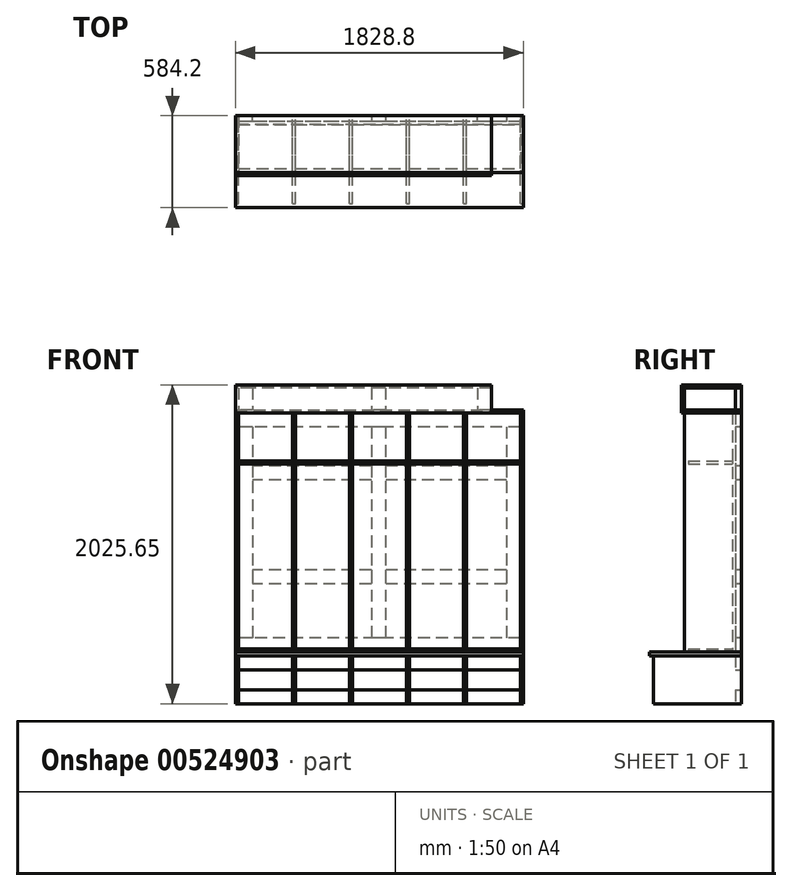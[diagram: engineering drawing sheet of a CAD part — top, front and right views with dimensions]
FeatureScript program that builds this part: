
annotation { "Feature Type Name" : "Feature", "Feature Type Description" : "" }
export const myFeature = defineFeature(function(context is Context, id is Id, definition is map)
    precondition{}
    {
        {
            var Q0;
            Q0=qCreatedBy(makeId("Front.planeOp"),FACE);
            var sketch = newSketch(context, id + "F0", { "sketchPlane" : qUnion([Q0])});
            skLineSegment(sketch, "E0.bottom", {"start": v(-620.12, 1849.45) * mm, "end": v(-601.07, 1849.45) * mm});
            skLineSegment(sketch, "E0.left", {"start": v(-620.12, 1849.45) * mm, "end": v(-620.12, 330.2) * mm});
            skLineSegment(sketch, "E0.right", {"start": v(-601.07, 1849.45) * mm, "end": v(-601.07, 330.2) * mm});
            skLineSegment(sketch, "E1.bottom", {"start": v(-258.17, 1849.45) * mm, "end": v(-239.12, 1849.45) * mm});
            skLineSegment(sketch, "E1.left", {"start": v(-258.17, 1849.45) * mm, "end": v(-258.17, 330.2) * mm});
            skLineSegment(sketch, "E1.right", {"start": v(-239.12, 1849.45) * mm, "end": v(-239.12, 330.2) * mm});
            skLineSegment(sketch, "E2.bottom", {"start": v(103.78, 1849.45) * mm, "end": v(122.83, 1849.45) * mm});
            skLineSegment(sketch, "E2.left", {"start": v(103.78, 1849.45) * mm, "end": v(103.78, 330.2) * mm});
            skLineSegment(sketch, "E2.right", {"start": v(122.83, 1849.45) * mm, "end": v(122.83, 330.2) * mm});
            skLineSegment(sketch, "E3.bottom", {"start": v(465.73, 1849.45) * mm, "end": v(484.78, 1849.45) * mm});
            skLineSegment(sketch, "E3.left", {"start": v(465.73, 1849.45) * mm, "end": v(465.73, 330.2) * mm});
            skLineSegment(sketch, "E3.right", {"start": v(484.78, 1849.45) * mm, "end": v(484.78, 330.2) * mm});
            skLineSegment(sketch, "E4.trimOffspring", {"start": v(465.73, 330.2) * mm, "end": v(484.78, 330.2) * mm});
            skLineSegment(sketch, "E5.trimOffspring", {"start": v(103.78, 330.2) * mm, "end": v(122.83, 330.2) * mm});
            skLineSegment(sketch, "E6.trimOffspring", {"start": v(-258.17, 330.2) * mm, "end": v(-239.12, 330.2) * mm});
            skLineSegment(sketch, "E7.trimOffspring", {"start": v(-620.12, 330.2) * mm, "end": v(-601.07, 330.2) * mm});
            skSolve(sketch);
        }
        {
            var Q0;
            Q0 = qSketchRegion(id + "F0", true);
            extrude(context, id + "F1", {"entities" : qUnion([Q0]), "depth" : 285.75 * mm, "offsetDistance" : 25.4 * mm, "hasSecondDirection" : true, "secondDirectionOppositeDirection" : true, "secondDirectionDepth" : 19.05 * mm});
        }
        {
            var Q0;
            Q0=qCreatedBy(makeId("Front.planeOp"),FACE);
            var sketch = newSketch(context, id + "F2", { "sketchPlane" : qUnion([Q0])});
            skLineSegment(sketch, "E8.bottom", {"start": v(-982.07, 330.2) * mm, "end": v(846.73, 330.2) * mm});
            skLineSegment(sketch, "E8.top", {"start": v(-982.07, 304.8) * mm, "end": v(846.73, 304.8) * mm});
            skLineSegment(sketch, "E8.left", {"start": v(-982.07, 330.2) * mm, "end": v(-982.07, 304.8) * mm});
            skLineSegment(sketch, "E8.right", {"start": v(846.73, 330.2) * mm, "end": v(846.73, 304.8) * mm});
            skSolve(sketch);
        }
        {
            var Q0;
            Q0 = qSketchRegion(id + "F2", true);
            extrude(context, id + "F3", {"entities" : qUnion([Q0]), "oppositeDirection" : true, "depth" : 76.2 * mm, "offsetDistance" : 25.4 * mm, "hasSecondDirection" : true, "secondDirectionOppositeDirection" : false, "secondDirectionDepth" : 508 * mm});
        }
        {
            var Q0;
            Q0=qCreatedBy(makeId("Front.planeOp"),FACE);
            var sketch = newSketch(context, id + "F4", { "sketchPlane" : qUnion([Q0])});
            skLineSegment(sketch, "E9.bottom", {"start": v(-982.07, 304.8) * mm, "end": v(-963.02, 304.8) * mm});
            skLineSegment(sketch, "E9.top", {"start": v(-982.07, 0) * mm, "end": v(-963.02, 0) * mm});
            skLineSegment(sketch, "E9.left", {"start": v(-982.07, 304.8) * mm, "end": v(-982.07, 0) * mm});
            skLineSegment(sketch, "E9.right", {"start": v(-963.02, 304.8) * mm, "end": v(-963.02, 0) * mm});
            skLineSegment(sketch, "E10.bottom", {"start": v(-620.12, 304.8) * mm, "end": v(-601.07, 304.8) * mm});
            skLineSegment(sketch, "E10.top", {"start": v(-620.12, 0) * mm, "end": v(-601.07, 0) * mm});
            skLineSegment(sketch, "E10.left", {"start": v(-620.12, 304.8) * mm, "end": v(-620.12, 0) * mm});
            skLineSegment(sketch, "E10.right", {"start": v(-601.07, 304.8) * mm, "end": v(-601.07, 0) * mm});
            skLineSegment(sketch, "E11.bottom", {"start": v(-258.17, 304.8) * mm, "end": v(-239.12, 304.8) * mm});
            skLineSegment(sketch, "E11.top", {"start": v(-258.17, 0) * mm, "end": v(-239.12, 0) * mm});
            skLineSegment(sketch, "E11.left", {"start": v(-258.17, 304.8) * mm, "end": v(-258.17, 0) * mm});
            skLineSegment(sketch, "E11.right", {"start": v(-239.12, 304.8) * mm, "end": v(-239.12, 0) * mm});
            skLineSegment(sketch, "E12.bottom", {"start": v(103.78, 304.8) * mm, "end": v(122.83, 304.8) * mm});
            skLineSegment(sketch, "E12.top", {"start": v(103.78, 0) * mm, "end": v(122.83, 0) * mm});
            skLineSegment(sketch, "E12.left", {"start": v(103.78, 304.8) * mm, "end": v(103.78, 0) * mm});
            skLineSegment(sketch, "E12.right", {"start": v(122.83, 304.8) * mm, "end": v(122.83, 0) * mm});
            skLineSegment(sketch, "E13.bottom", {"start": v(465.73, 304.8) * mm, "end": v(484.78, 304.8) * mm});
            skLineSegment(sketch, "E13.top", {"start": v(465.73, 0) * mm, "end": v(484.78, 0) * mm});
            skLineSegment(sketch, "E13.left", {"start": v(465.73, 304.8) * mm, "end": v(465.73, 0) * mm});
            skLineSegment(sketch, "E13.right", {"start": v(484.78, 304.8) * mm, "end": v(484.78, 0) * mm});
            skLineSegment(sketch, "E14.bottom", {"start": v(827.68, 304.8) * mm, "end": v(846.73, 304.8) * mm});
            skLineSegment(sketch, "E14.top", {"start": v(827.68, 0) * mm, "end": v(846.73, 0) * mm});
            skLineSegment(sketch, "E14.left", {"start": v(827.68, 304.8) * mm, "end": v(827.68, 0) * mm});
            skLineSegment(sketch, "E14.right", {"start": v(846.73, 304.8) * mm, "end": v(846.73, 0) * mm});
            skSolve(sketch);
        }
        {
            var Q0;
            Q0 = qSketchRegion(id + "F4", true);
            extrude(context, id + "F5", {"entities" : qUnion([Q0]), "depth" : 482.6 * mm, "offsetDistance" : 25.4 * mm, "hasSecondDirection" : true, "secondDirectionOppositeDirection" : true, "secondDirectionDepth" : 76.2 * mm});
        }
        {
            var Q0;
            Q0=makeQuery(id+"F5.opExtrude","CAP_FACE",FACE,{"disambiguationData":[OSD([sQuery(id+"F4.wireOp",EDGE,"E14.bottom"),sQuery(id+"F4.wireOp",EDGE,"E14.top"),sQuery(id+"F4.wireOp",EDGE,"E14.left"),sQuery(id+"F4.wireOp",EDGE,"E14.right")])],"isStart":true});
            var sketch = newSketch(context, id + "F6", { "sketchPlane" : qUnion([Q0])});
            skLineSegment(sketch, "E15.bottom", {"start": v(-827.68, 88.9) * mm, "end": v(963.02, 88.9) * mm});
            skLineSegment(sketch, "E15.top", {"start": v(-827.68, 0) * mm, "end": v(963.02, 0) * mm});
            skLineSegment(sketch, "E15.left", {"start": v(-827.68, 88.9) * mm, "end": v(-827.68, 0) * mm});
            skLineSegment(sketch, "E15.right", {"start": v(963.02, 88.9) * mm, "end": v(963.02, 0) * mm});
            skLineSegment(sketch, "E16.bottom", {"start": v(-827.68, 419.1) * mm, "end": v(963.02, 419.1) * mm});
            skLineSegment(sketch, "E16.top", {"start": v(-827.68, 330.2) * mm, "end": v(963.02, 330.2) * mm});
            skLineSegment(sketch, "E17.top", {"start": v(-827.68, 1758.95) * mm, "end": v(963.02, 1758.95) * mm});
            skLineSegment(sketch, "E18", {"start": v(-827.68, 1847.85) * mm, "end": v(-827.68, 1758.95) * mm});
            skLineSegment(sketch, "E19", {"start": v(963.02, 1847.85) * mm, "end": v(963.02, 1758.95) * mm});
            skLineSegment(sketch, "E20.trimOffspring", {"start": v(963.02, 419.1) * mm, "end": v(963.02, 330.2) * mm});
            skLineSegment(sketch, "E21.trimOffspring", {"start": v(-827.68, 419.1) * mm, "end": v(-827.68, 330.2) * mm});
            skLineSegment(sketch, "E22", {"start": v(-827.68, 1847.85) * mm, "end": v(963.02, 1847.85) * mm});
            skLineSegment(sketch, "E23.bottom", {"start": v(-827.68, 304.8) * mm, "end": v(963.02, 304.8) * mm});
            skLineSegment(sketch, "E23.top", {"start": v(-827.68, 215.9) * mm, "end": v(963.02, 215.9) * mm});
            skLineSegment(sketch, "E23.left", {"start": v(-827.68, 304.8) * mm, "end": v(-827.68, 215.9) * mm});
            skLineSegment(sketch, "E23.right", {"start": v(963.02, 304.8) * mm, "end": v(963.02, 215.9) * mm});
            skSolve(sketch);
        }
        {
            var Q0;
            Q0=makeQuery(id+"F6.imprint","IMPRINT",FACE,{"disambiguationData":[TD([[makeQuery(id+"F6.imprint","IMPRINT",EDGE,{"derivedFrom":sQuery(id+"F6.wireOp",EDGE,"E17.top")}),1.0]])]});
            var Q1;
            Q1=makeQuery(id+"F6.imprint","IMPRINT",FACE,{"disambiguationData":[TD([[makeQuery(id+"F6.imprint","IMPRINT",EDGE,{"derivedFrom":sQuery(id+"F6.wireOp",EDGE,"E16.bottom")}),-1.0]])]});
            var Q2;
            Q2=makeQuery(id+"F6.imprint","IMPRINT",FACE,{"disambiguationData":[TD([[makeQuery(id+"F6.imprint","IMPRINT",EDGE,{"derivedFrom":sQuery(id+"F6.wireOp",EDGE,"E15.bottom")}),-1.0]])]});
            var Q3;
            Q3=makeQuery(id+"F6.imprint","IMPRINT",FACE,{"disambiguationData":[TD([[makeQuery(id+"F6.imprint","IMPRINT",EDGE,{"derivedFrom":sQuery(id+"F6.wireOp",EDGE,"E23.bottom")}),-1.0]])]});
            extrude(context, id + "F7", {"entities" : qUnion([Q0, Q1, Q2, Q3]), "oppositeDirection" : true, "depth" : 38.1 * mm, "offsetDistance" : 25.4 * mm});
        }
        {
            var Q0;
            Q0=makeQuery(id+"F1.opExtrude","CAP_FACE",FACE,{"disambiguationData":[OSD([sQuery(id+"F0.wireOp",EDGE,"E0.bottom"),sQuery(id+"F0.wireOp",EDGE,"E0.left"),sQuery(id+"F0.wireOp",EDGE,"E0.right"),sQuery(id+"F0.wireOp",EDGE,"E7.trimOffspring")])],"isStart":false});
            var sketch = newSketch(context, id + "F8", { "sketchPlane" : qUnion([Q0])});
            skLineSegment(sketch, "E24.bottom", {"start": v(-963.02, 330.2) * mm, "end": v(-982.07, 330.2) * mm});
            skLineSegment(sketch, "E24.top", {"start": v(-963.02, 1847.85) * mm, "end": v(-982.07, 1847.85) * mm});
            skLineSegment(sketch, "E24.left", {"start": v(-963.02, 330.2) * mm, "end": v(-963.02, 1847.85) * mm});
            skLineSegment(sketch, "E24.right", {"start": v(-982.07, 330.2) * mm, "end": v(-982.07, 1847.85) * mm});
            skLineSegment(sketch, "E25.bottom", {"start": v(827.68, 330.2) * mm, "end": v(846.73, 330.2) * mm});
            skLineSegment(sketch, "E25.top", {"start": v(827.68, 1847.85) * mm, "end": v(846.73, 1847.85) * mm});
            skLineSegment(sketch, "E25.left", {"start": v(827.68, 330.2) * mm, "end": v(827.68, 1847.85) * mm});
            skLineSegment(sketch, "E25.right", {"start": v(846.73, 330.2) * mm, "end": v(846.73, 1847.85) * mm});
            skSolve(sketch);
        }
        {
            var Q0;
            Q0 = qSketchRegion(id + "F8", true);
            extrude(context, id + "F9", {"entities" : qUnion([Q0]), "oppositeDirection" : true, "depth" : 361.95 * mm, "offsetDistance" : 25.4 * mm});
        }
        {
            var Q0;
            Q0=makeQuery(id+"F3.opExtrude","SWEPT_FACE",FACE,{"disambiguationData":[OSD([sQuery(id+"F2.wireOp",EDGE,"E8.bottom")])]});
            var sketch = newSketch(context, id + "F10", { "sketchPlane" : qUnion([Q0])});
            skLineSegment(sketch, "E26.bottom", {"start": v(-963.02, 38.1) * mm, "end": v(827.68, 38.1) * mm});
            skLineSegment(sketch, "E26.top", {"start": v(-963.02, 19.05) * mm, "end": v(827.68, 19.05) * mm});
            skLineSegment(sketch, "E26.left", {"start": v(-963.02, 38.1) * mm, "end": v(-963.02, 19.05) * mm});
            skLineSegment(sketch, "E26.right", {"start": v(827.68, 38.1) * mm, "end": v(827.68, 19.05) * mm});
            skSolve(sketch);
        }
        {
            var Q0;
            Q0=makeQuery(id+"F10.imprint","IMPRINT",FACE,{"disambiguationData":[TD([[makeQuery(id+"F10.imprint","IMPRINT",EDGE,{"derivedFrom":sQuery(id+"F10.wireOp",EDGE,"E26.bottom")}),-1.0]])]});
            var Q1;
            Q1=makeQuery(id+"F7.opExtrude","SWEPT_FACE",FACE,{"disambiguationData":[OSD([sQuery(id+"F6.wireOp",EDGE,"E22")])]});
            extrude(context, id + "F11", {"entities" : qUnion([Q0]), "endBound" : BoundingType.UP_TO_SURFACE, "depth" : 25.4 * mm, "endBoundEntityFace" : qUnion([Q1]), "offsetDistance" : 25.4 * mm});
        }
        {
            var Q0;
            Q0=makeQuery(id+"F11.opExtrude","SWEPT_FACE",FACE,{"disambiguationData":[OSD([sQuery(id+"F10.wireOp",EDGE,"E26.top")])]});
            var sketch = newSketch(context, id + "F12", { "sketchPlane" : qUnion([Q0])});
            skLineSegment(sketch, "E27.bottom", {"start": v(-963.02, 1543.05) * mm, "end": v(-620.12, 1543.05) * mm});
            skLineSegment(sketch, "E27.top", {"start": v(-963.02, 1524) * mm, "end": v(-620.12, 1524) * mm});
            skLineSegment(sketch, "E27.left", {"start": v(-963.02, 1543.05) * mm, "end": v(-963.02, 1524) * mm});
            skLineSegment(sketch, "E27.right", {"start": v(-620.12, 1543.05) * mm, "end": v(-620.12, 1524) * mm});
            skLineSegment(sketch, "E28.bottom", {"start": v(-601.07, 1543.05) * mm, "end": v(-258.17, 1543.05) * mm});
            skLineSegment(sketch, "E28.top", {"start": v(-601.07, 1524) * mm, "end": v(-258.17, 1524) * mm});
            skLineSegment(sketch, "E28.left", {"start": v(-601.07, 1543.05) * mm, "end": v(-601.07, 1524) * mm});
            skLineSegment(sketch, "E28.right", {"start": v(-258.17, 1543.05) * mm, "end": v(-258.17, 1524) * mm});
            skLineSegment(sketch, "E29.bottom", {"start": v(-239.12, 1543.05) * mm, "end": v(103.78, 1543.05) * mm});
            skLineSegment(sketch, "E29.top", {"start": v(-239.12, 1524) * mm, "end": v(103.78, 1524) * mm});
            skLineSegment(sketch, "E29.left", {"start": v(-239.12, 1543.05) * mm, "end": v(-239.12, 1524) * mm});
            skLineSegment(sketch, "E29.right", {"start": v(103.78, 1543.05) * mm, "end": v(103.78, 1524) * mm});
            skLineSegment(sketch, "E30.bottom", {"start": v(122.83, 1543.05) * mm, "end": v(465.73, 1543.05) * mm});
            skLineSegment(sketch, "E30.top", {"start": v(122.83, 1524) * mm, "end": v(465.73, 1524) * mm});
            skLineSegment(sketch, "E30.left", {"start": v(122.83, 1543.05) * mm, "end": v(122.83, 1524) * mm});
            skLineSegment(sketch, "E30.right", {"start": v(465.73, 1543.05) * mm, "end": v(465.73, 1524) * mm});
            skLineSegment(sketch, "E31.bottom", {"start": v(484.78, 1543.05) * mm, "end": v(827.68, 1543.05) * mm});
            skLineSegment(sketch, "E31.top", {"start": v(484.78, 1524) * mm, "end": v(827.68, 1524) * mm});
            skLineSegment(sketch, "E31.left", {"start": v(484.78, 1543.05) * mm, "end": v(484.78, 1524) * mm});
            skLineSegment(sketch, "E31.right", {"start": v(827.68, 1543.05) * mm, "end": v(827.68, 1524) * mm});
            skSolve(sketch);
        }
        {
            var Q0;
            Q0 = qSketchRegion(id + "F12", true);
            extrude(context, id + "F13", {"entities" : qUnion([Q0]), "depth" : 279.4 * mm, "offsetDistance" : 25.4 * mm});
        }
        {
            var Q0;
            Q0=makeQuery(id+"F9.opExtrude","CAP_FACE",FACE,{"disambiguationData":[OSD([sQuery(id+"F8.wireOp",EDGE,"E24.bottom"),sQuery(id+"F8.wireOp",EDGE,"E24.top"),sQuery(id+"F8.wireOp",EDGE,"E24.left"),sQuery(id+"F8.wireOp",EDGE,"E24.right")])],"isStart":true});
            var sketch = newSketch(context, id + "F14", { "sketchPlane" : qUnion([Q0])});
            skLineSegment(sketch, "E32.bottom", {"start": v(-982.07, 1847.85) * mm, "end": v(643.53, 1847.85) * mm});
            skLineSegment(sketch, "E32.top", {"start": v(-982.07, 2025.65) * mm, "end": v(643.53, 2025.65) * mm});
            skLineSegment(sketch, "E32.left", {"start": v(-982.07, 1847.85) * mm, "end": v(-982.07, 2025.65) * mm});
            skLineSegment(sketch, "E32.right", {"start": v(643.53, 1847.85) * mm, "end": v(643.53, 2025.65) * mm});
            skSolve(sketch);
        }
        {
            var Q0;
            Q0=makeQuery(id+"F14.imprint","IMPRINT",FACE,{"disambiguationData":[TD([[makeQuery(id+"F14.imprint","IMPRINT",EDGE,{"derivedFrom":sQuery(id+"F14.wireOp",EDGE,"E32.top")}),-1.0]])]});
            extrude(context, id + "F15", {"entities" : qUnion([Q0]), "depth" : 19.05 * mm, "offsetDistance" : 25.4 * mm});
        }
        {
            var Q0;
            Q0=makeQuery(id+"F15.opExtrude","CAP_FACE",FACE,{"disambiguationData":[OSD([sQuery(id+"F14.wireOp",EDGE,"E32.bottom"),sQuery(id+"F14.wireOp",EDGE,"E32.top"),sQuery(id+"F14.wireOp",EDGE,"E32.left"),sQuery(id+"F14.wireOp",EDGE,"E32.right")])],"isStart":true});
            var sketch = newSketch(context, id + "F16", { "sketchPlane" : qUnion([Q0])});
            skLineSegment(sketch, "E33.bottom", {"start": v(-643.53, 2025.65) * mm, "end": v(982.07, 2025.65) * mm});
            skLineSegment(sketch, "E33.top", {"start": v(-643.53, 2006.6) * mm, "end": v(982.07, 2006.6) * mm});
            skLineSegment(sketch, "E33.left", {"start": v(-643.53, 2025.65) * mm, "end": v(-643.53, 2006.6) * mm});
            skLineSegment(sketch, "E33.right", {"start": v(982.07, 2025.65) * mm, "end": v(982.07, 2006.6) * mm});
            skLineSegment(sketch, "E34.bottom", {"start": v(982.07, 1847.85) * mm, "end": v(-846.73, 1847.85) * mm});
            skLineSegment(sketch, "E34.top", {"start": v(982.07, 1866.9) * mm, "end": v(-846.73, 1866.9) * mm});
            skLineSegment(sketch, "E34.left", {"start": v(982.07, 1847.85) * mm, "end": v(982.07, 1866.9) * mm});
            skLineSegment(sketch, "E34.right", {"start": v(-846.73, 1847.85) * mm, "end": v(-846.73, 1866.9) * mm});
            skSolve(sketch);
        }
        {
            var Q0;
            Q0 = qSketchRegion(id + "F16", true);
            var Q1;
            Q1=makeQuery(id+"F7.opExtrude","CAP_FACE",FACE,{"disambiguationData":[OSD([sQuery(id+"F6.wireOp",EDGE,"E17.top"),sQuery(id+"F6.wireOp",EDGE,"E18"),sQuery(id+"F6.wireOp",EDGE,"E19"),sQuery(id+"F6.wireOp",EDGE,"E22")])],"isStart":true});
            extrude(context, id + "F17", {"entities" : qUnion([Q0]), "endBound" : BoundingType.UP_TO_SURFACE, "depth" : 285.75 * mm, "endBoundEntityFace" : qUnion([Q1]), "offsetDistance" : 25.4 * mm});
        }
        {
            var Q0;
            Q0=makeQuery(id+"F11.opExtrude","SWEPT_FACE",FACE,{"disambiguationData":[OSD([sQuery(id+"F10.wireOp",EDGE,"E26.bottom")])]});
            var sketch = newSketch(context, id + "F18", { "sketchPlane" : qUnion([Q0])});
            skLineSegment(sketch, "E35.bottom", {"start": v(-827.68, 1758.95) * mm, "end": v(-738.78, 1758.95) * mm});
            skLineSegment(sketch, "E35.top", {"start": v(-827.68, 419.1) * mm, "end": v(-738.78, 419.1) * mm});
            skLineSegment(sketch, "E35.left", {"start": v(-827.68, 1758.95) * mm, "end": v(-827.68, 419.1) * mm});
            skLineSegment(sketch, "E35.right", {"start": v(-738.78, 1758.95) * mm, "end": v(-738.78, 419.1) * mm});
            skLineSegment(sketch, "E36.bottom", {"start": v(874.12, 1758.95) * mm, "end": v(963.02, 1758.95) * mm});
            skLineSegment(sketch, "E36.top", {"start": v(874.12, 419.1) * mm, "end": v(963.02, 419.1) * mm});
            skLineSegment(sketch, "E36.left", {"start": v(874.12, 1758.95) * mm, "end": v(874.12, 419.1) * mm});
            skLineSegment(sketch, "E36.right", {"start": v(963.02, 1758.95) * mm, "end": v(963.02, 419.1) * mm});
            skLineSegment(sketch, "E37.bottom", {"start": v(29.57, 1758.95) * mm, "end": v(118.47, 1758.95) * mm});
            skLineSegment(sketch, "E37.top", {"start": v(29.57, 419.1) * mm, "end": v(118.47, 419.1) * mm});
            skLineSegment(sketch, "E37.left", {"start": v(29.57, 1758.95) * mm, "end": v(29.57, 419.1) * mm});
            skLineSegment(sketch, "E37.right", {"start": v(118.47, 1758.95) * mm, "end": v(118.47, 419.1) * mm});
            skSolve(sketch);
        }
        {
            var Q0;
            Q0 = qSketchRegion(id + "F18", true);
            extrude(context, id + "F19", {"entities" : qUnion([Q0]), "depth" : 38.1 * mm, "offsetDistance" : 25.4 * mm});
        }
        {
            var Q0;
            Q0=makeQuery(id+"F11.opExtrude","SWEPT_FACE",FACE,{"disambiguationData":[OSD([sQuery(id+"F10.wireOp",EDGE,"E26.bottom")])]});
            var sketch = newSketch(context, id + "F20", { "sketchPlane" : qUnion([Q0])});
            skLineSegment(sketch, "E38.bottom", {"start": v(-738.78, 1511.3) * mm, "end": v(29.57, 1511.3) * mm});
            skLineSegment(sketch, "E38.top", {"start": v(-738.78, 1422.4) * mm, "end": v(29.57, 1422.4) * mm});
            skLineSegment(sketch, "E38.left", {"start": v(-738.78, 1511.3) * mm, "end": v(-738.78, 1422.4) * mm});
            skLineSegment(sketch, "E39.bottom", {"start": v(118.47, 1511.3) * mm, "end": v(874.12, 1511.3) * mm});
            skLineSegment(sketch, "E39.top", {"start": v(118.47, 1422.4) * mm, "end": v(874.12, 1422.4) * mm});
            skLineSegment(sketch, "E39.left", {"start": v(118.47, 1511.3) * mm, "end": v(118.47, 1422.4) * mm});
            skLineSegment(sketch, "E39.right", {"start": v(874.12, 1511.3) * mm, "end": v(874.12, 1422.4) * mm});
            skLineSegment(sketch, "E40.bottom", {"start": v(-738.78, 850.9) * mm, "end": v(29.57, 850.9) * mm});
            skLineSegment(sketch, "E40.top", {"start": v(-738.78, 762) * mm, "end": v(29.57, 762) * mm});
            skLineSegment(sketch, "E40.left", {"start": v(-738.78, 850.9) * mm, "end": v(-738.78, 762) * mm});
            skLineSegment(sketch, "E40.right", {"start": v(29.57, 850.9) * mm, "end": v(29.57, 762) * mm});
            skLineSegment(sketch, "E41.bottom", {"start": v(118.47, 850.9) * mm, "end": v(874.12, 850.9) * mm});
            skLineSegment(sketch, "E41.top", {"start": v(118.47, 762) * mm, "end": v(874.12, 762) * mm});
            skLineSegment(sketch, "E41.left", {"start": v(118.47, 850.9) * mm, "end": v(118.47, 762) * mm});
            skLineSegment(sketch, "E41.right", {"start": v(874.12, 850.9) * mm, "end": v(874.12, 762) * mm});
            skLineSegment(sketch, "E42", {"start": v(29.57, 1511.3) * mm, "end": v(29.57, 1422.4) * mm});
            skSolve(sketch);
        }
        {
            var Q0;
            Q0 = qSketchRegion(id + "F20", true);
            extrude(context, id + "F21", {"entities" : qUnion([Q0]), "depth" : 38.1 * mm, "offsetDistance" : 25.4 * mm});
        }
        {
            var Q0;
            Q0=makeQuery(id+"F7.opExtrude","CAP_FACE",FACE,{"disambiguationData":[OSD([sQuery(id+"F6.wireOp",EDGE,"E17.top"),sQuery(id+"F6.wireOp",EDGE,"E18"),sQuery(id+"F6.wireOp",EDGE,"E19"),sQuery(id+"F6.wireOp",EDGE,"E22")])],"isStart":true});
            var sketch = newSketch(context, id + "F22", { "sketchPlane" : qUnion([Q0])});
            skLineSegment(sketch, "E43.bottom", {"start": v(29.57, 2006.6) * mm, "end": v(118.47, 2006.6) * mm});
            skLineSegment(sketch, "E43.top", {"start": v(29.57, 1866.9) * mm, "end": v(118.47, 1866.9) * mm});
            skLineSegment(sketch, "E43.left", {"start": v(29.57, 2006.6) * mm, "end": v(29.57, 1866.9) * mm});
            skLineSegment(sketch, "E43.right", {"start": v(118.47, 2006.6) * mm, "end": v(118.47, 1866.9) * mm});
            skLineSegment(sketch, "E44.bottom", {"start": v(874.12, 2006.6) * mm, "end": v(963.02, 2006.6) * mm});
            skLineSegment(sketch, "E44.top", {"start": v(874.12, 1866.9) * mm, "end": v(963.02, 1866.9) * mm});
            skLineSegment(sketch, "E44.left", {"start": v(874.12, 2006.6) * mm, "end": v(874.12, 1866.9) * mm});
            skLineSegment(sketch, "E44.right", {"start": v(963.02, 2006.6) * mm, "end": v(963.02, 1866.9) * mm});
            skLineSegment(sketch, "E45.bottom", {"start": v(-643.53, 2006.6) * mm, "end": v(-554.63, 2006.6) * mm});
            skLineSegment(sketch, "E45.top", {"start": v(-643.53, 1866.9) * mm, "end": v(-554.63, 1866.9) * mm});
            skLineSegment(sketch, "E45.left", {"start": v(-643.53, 2006.6) * mm, "end": v(-643.53, 1866.9) * mm});
            skLineSegment(sketch, "E45.right", {"start": v(-554.63, 2006.6) * mm, "end": v(-554.63, 1866.9) * mm});
            skSolve(sketch);
        }
        {
            var Q0;
            Q0 = qSketchRegion(id + "F22", true);
            extrude(context, id + "F23", {"entities" : qUnion([Q0]), "oppositeDirection" : true, "depth" : 38.1 * mm, "offsetDistance" : 25.4 * mm});
        }
        {
            var Q0;
            Q0=makeQuery(id+"F11.opExtrude","SWEPT_FACE",FACE,{"disambiguationData":[OSD([sQuery(id+"F10.wireOp",EDGE,"E26.top")])]});
            var sketch = newSketch(context, id + "F24", { "sketchPlane" : qUnion([Q0])});
            skLineSegment(sketch, "E46.bottom", {"start": v(-963.02, 349.25) * mm, "end": v(-620.12, 349.25) * mm});
            skLineSegment(sketch, "E46.top", {"start": v(-963.02, 330.2) * mm, "end": v(-620.12, 330.2) * mm});
            skLineSegment(sketch, "E46.left", {"start": v(-963.02, 349.25) * mm, "end": v(-963.02, 330.2) * mm});
            skLineSegment(sketch, "E46.right", {"start": v(-620.12, 349.25) * mm, "end": v(-620.12, 330.2) * mm});
            skLineSegment(sketch, "E47.bottom", {"start": v(-239.12, 349.25) * mm, "end": v(103.78, 349.25) * mm});
            skLineSegment(sketch, "E47.top", {"start": v(-239.12, 330.2) * mm, "end": v(103.78, 330.2) * mm});
            skLineSegment(sketch, "E47.left", {"start": v(-239.12, 349.25) * mm, "end": v(-239.12, 330.2) * mm});
            skLineSegment(sketch, "E47.right", {"start": v(103.78, 349.25) * mm, "end": v(103.78, 330.2) * mm});
            skLineSegment(sketch, "E48.bottom", {"start": v(484.78, 349.25) * mm, "end": v(827.68, 349.25) * mm});
            skLineSegment(sketch, "E48.top", {"start": v(484.78, 330.2) * mm, "end": v(827.68, 330.2) * mm});
            skLineSegment(sketch, "E48.left", {"start": v(484.78, 349.25) * mm, "end": v(484.78, 330.2) * mm});
            skLineSegment(sketch, "E48.right", {"start": v(827.68, 349.25) * mm, "end": v(827.68, 330.2) * mm});
            skLineSegment(sketch, "E49.bottom", {"start": v(122.83, 349.25) * mm, "end": v(465.73, 349.25) * mm});
            skLineSegment(sketch, "E49.top", {"start": v(122.83, 330.2) * mm, "end": v(465.73, 330.2) * mm});
            skLineSegment(sketch, "E49.left", {"start": v(122.83, 349.25) * mm, "end": v(122.83, 330.2) * mm});
            skLineSegment(sketch, "E49.right", {"start": v(465.73, 349.25) * mm, "end": v(465.73, 330.2) * mm});
            skLineSegment(sketch, "E50.bottom", {"start": v(-601.07, 349.25) * mm, "end": v(-258.17, 349.25) * mm});
            skLineSegment(sketch, "E50.top", {"start": v(-601.07, 330.2) * mm, "end": v(-258.17, 330.2) * mm});
            skLineSegment(sketch, "E50.left", {"start": v(-601.07, 349.25) * mm, "end": v(-601.07, 330.2) * mm});
            skLineSegment(sketch, "E50.right", {"start": v(-258.17, 349.25) * mm, "end": v(-258.17, 330.2) * mm});
            skSolve(sketch);
        }
        {
            var Q0;
            Q0 = qSketchRegion(id + "F24", true);
            var Q1;
            Q1=makeQuery(id+"F13.opExtrude","CAP_FACE",FACE,{"disambiguationData":[OSD([sQuery(id+"F12.wireOp",EDGE,"E28.bottom"),sQuery(id+"F12.wireOp",EDGE,"E28.top"),sQuery(id+"F12.wireOp",EDGE,"E28.left"),sQuery(id+"F12.wireOp",EDGE,"E28.right")])],"isStart":false});
            extrude(context, id + "F25", {"entities" : qUnion([Q0]), "endBound" : BoundingType.UP_TO_SURFACE, "depth" : 25.4 * mm, "endBoundEntityFace" : qUnion([Q1]), "offsetDistance" : 25.4 * mm});
        }
    });
